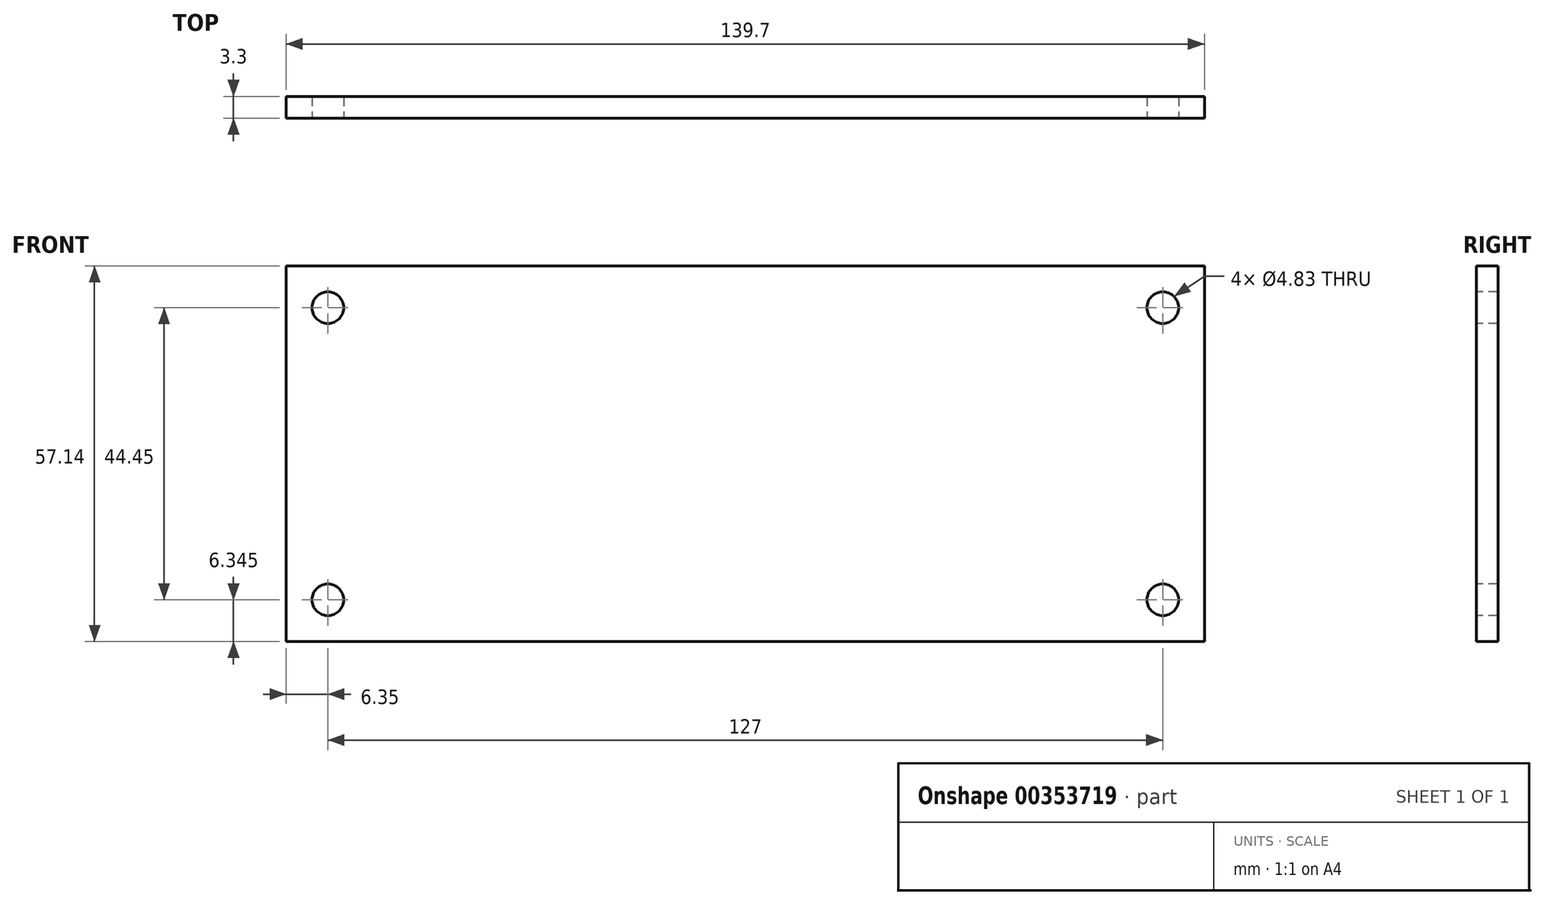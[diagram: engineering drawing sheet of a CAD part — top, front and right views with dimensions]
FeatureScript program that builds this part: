
annotation { "Feature Type Name" : "Feature", "Feature Type Description" : "" }
export const myFeature = defineFeature(function(context is Context, id is Id, definition is map)
    precondition{}
    {
        {
            var Q0;
            Q0=qCreatedBy(makeId("Front.planeOp"),FACE);
            var sketch = newSketch(context, id + "F0", { "sketchPlane" : qUnion([Q0])});
            skLineSegment(sketch, "E0.bottom", {"start": v(-69.85, 28.58) * mm, "end": v(69.85, 28.58) * mm});
            skLineSegment(sketch, "E0.top", {"start": v(-69.85, -28.57) * mm, "end": v(69.85, -28.57) * mm});
            skLineSegment(sketch, "E0.left", {"start": v(-69.85, 28.58) * mm, "end": v(-69.85, -28.57) * mm});
            skLineSegment(sketch, "E0.right", {"start": v(69.85, 28.58) * mm, "end": v(69.85, -28.57) * mm});
            skPoint(sketch, "E0.middle", {"position": v(0, 0) * mm});
            skSolve(sketch);
        }
        {
            var Q0;
            Q0 = qSketchRegion(id + "F0", true);
            extrude(context, id + "F1", {"entities" : qUnion([Q0]), "depth" : 3.3 * mm, "symmetric" : true});
        }
        {
            var Q0;
            Q0=makeQuery(id+"F1.opExtrude","CAP_FACE",FACE,{"disambiguationData":[OSD([sQuery(id+"F0.wireOp",EDGE,"E0.bottom"),sQuery(id+"F0.wireOp",EDGE,"E0.top"),sQuery(id+"F0.wireOp",EDGE,"E0.left"),sQuery(id+"F0.wireOp",EDGE,"E0.right")])],"isStart":false});
            var sketch = newSketch(context, id + "F2", { "sketchPlane" : qUnion([Q0])});
            skLineSegment(sketch, "E1", {"start": v(-63.5, 28.58) * mm, "end": v(-63.5, 22.23) * mm, "construction": true});
            skLineSegment(sketch, "E2", {"start": v(-63.5, 22.23) * mm, "end": v(-69.85, 22.23) * mm, "construction": true});
            skLineSegment(sketch, "E3", {"start": v(63.5, 28.58) * mm, "end": v(63.5, 22.23) * mm, "construction": true});
            skLineSegment(sketch, "E4", {"start": v(63.5, 22.23) * mm, "end": v(69.85, 22.23) * mm, "construction": true});
            skLineSegment(sketch, "E5", {"start": v(69.85, -22.22) * mm, "end": v(63.5, -22.22) * mm, "construction": true});
            skLineSegment(sketch, "E6", {"start": v(63.5, -22.22) * mm, "end": v(63.5, -28.57) * mm, "construction": true});
            skLineSegment(sketch, "E7", {"start": v(-63.5, -28.57) * mm, "end": v(-63.5, -22.22) * mm, "construction": true});
            skLineSegment(sketch, "E8", {"start": v(-63.5, -22.22) * mm, "end": v(-69.85, -22.22) * mm, "construction": true});
            skCircle(sketch, "E9", {"center": v(-63.5, 22.23) * mm, "radius": 2.41 * mm});
            skCircle(sketch, "E10", {"center": v(-63.5, -22.22) * mm, "radius": 2.41 * mm});
            skCircle(sketch, "E11", {"center": v(63.5, -22.22) * mm, "radius": 2.41 * mm});
            skCircle(sketch, "E12", {"center": v(63.5, 22.23) * mm, "radius": 2.41 * mm});
            skSolve(sketch);
        }
        {
            var Q0;
            Q0 = qSketchRegion(id + "F2", true);
            extrude(context, id + "F3", {"entities" : qUnion([Q0]), "operationType" : NewBodyOperationType.REMOVE, "oppositeDirection" : true, "depth" : 25.4 * mm, "symmetric" : true});
        }
    });
